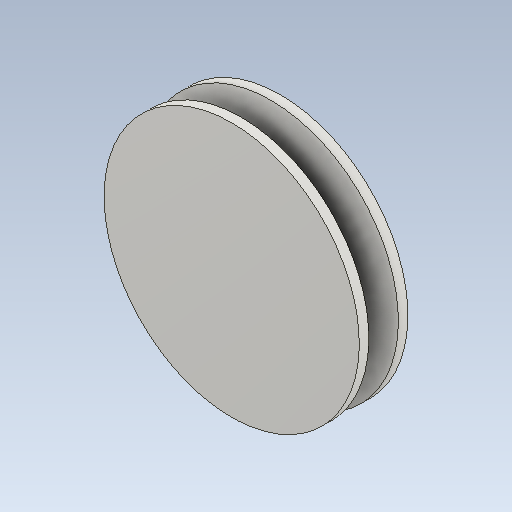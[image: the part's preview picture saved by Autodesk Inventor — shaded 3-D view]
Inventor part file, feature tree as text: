
AUTODESK INVENTOR PART (.ipt)
format: ipt  version: 2020.5 (Build 245400000, 400)  size: 131,072 bytes
history: native  units: mm (DEFAULTED — no unit token found)
features: other x3, fillet x2, sketch x1, pattern_linear x1
ambient origin geometry x8: Origin, YZ Plane, XZ Plane, XY Plane, X Axis, Y Axis, Z Axis, Center Point
bodies: Solid1 (feature_tree)
feature tree (7):
  sketch  "Boceto principal"  dims[d2=2.0mm d5=8.0mm d6=16.0mm d7=90.0deg d8=0.0mm d9=0.0mm d10=0.0mm d11=0.0mm d15=90.0deg d16=10.0mm d18=12.0mm d21=80.0mm d24=0.0mm d25=11.0mm d26=0.0mm d27=8.0mm]
  other  "Plano de correa"
  other  "Cuerpo"
  other  "Para ranuras"
  fillet  "Empalme externo"  Radius=8.5mm
  fillet  "Empalme interno"  Radius=5.934119mm
  pattern_linear  "Patrón para ranuras"  Spacing1=8.0mm  [1 undecoded]
note: 1 required parameter value undecoded (feature->parameter linkage not recoverable at this tier; creation-order binding heuristic only, values carry confidence <= 0.55)
